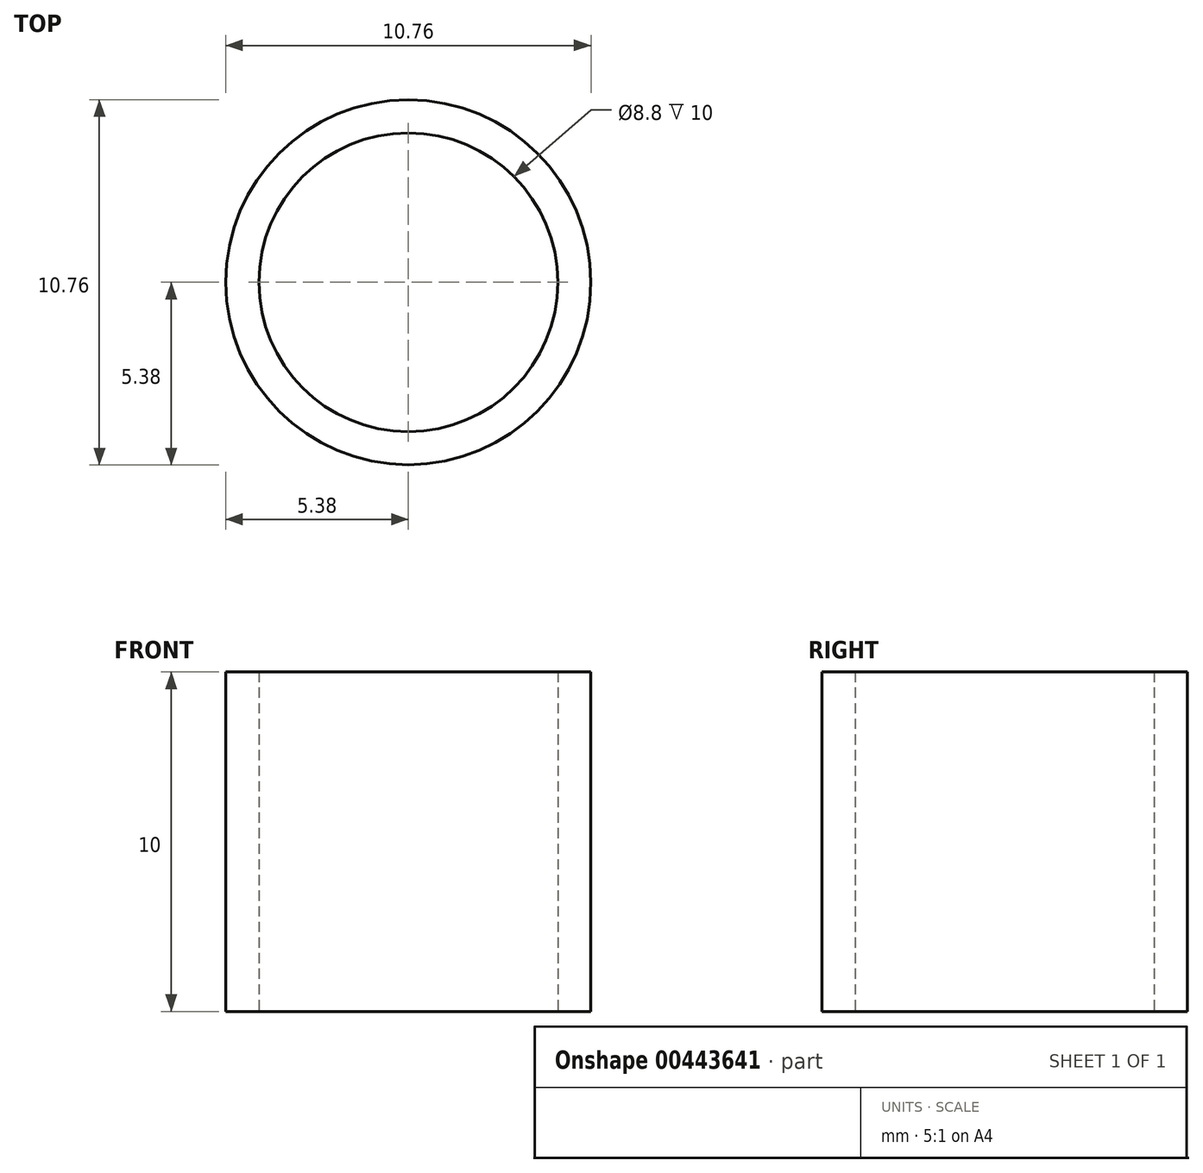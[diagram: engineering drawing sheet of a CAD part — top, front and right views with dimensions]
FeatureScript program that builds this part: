
annotation { "Feature Type Name" : "Feature", "Feature Type Description" : "" }
export const myFeature = defineFeature(function(context is Context, id is Id, definition is map)
    precondition{}
    {
        {
            var Q0;
            Q0=qCreatedBy(makeId("Top.planeOp"),FACE);
            var sketch = newSketch(context, id + "F0", { "sketchPlane" : qUnion([Q0])});
            skCircle(sketch, "E0", {"center": v(0, 0) * mm, "radius": 5.38 * mm});
            skCircle(sketch, "E1", {"center": v(0, 0) * mm, "radius": 4.4 * mm});
            skSolve(sketch);
        }
        {
            var Q0;
            Q0=makeQuery(id+"F0.imprint","IMPRINT",FACE,{"disambiguationData":[TD([[makeQuery(id+"F0.imprint","IMPRINT",EDGE,{"derivedFrom":sQuery(id+"F0.wireOp",EDGE,"E0")}),1.0]])]});
            extrude(context, id + "F1", {"entities" : qUnion([Q0]), "depth" : 10 * mm});
        }
    });
